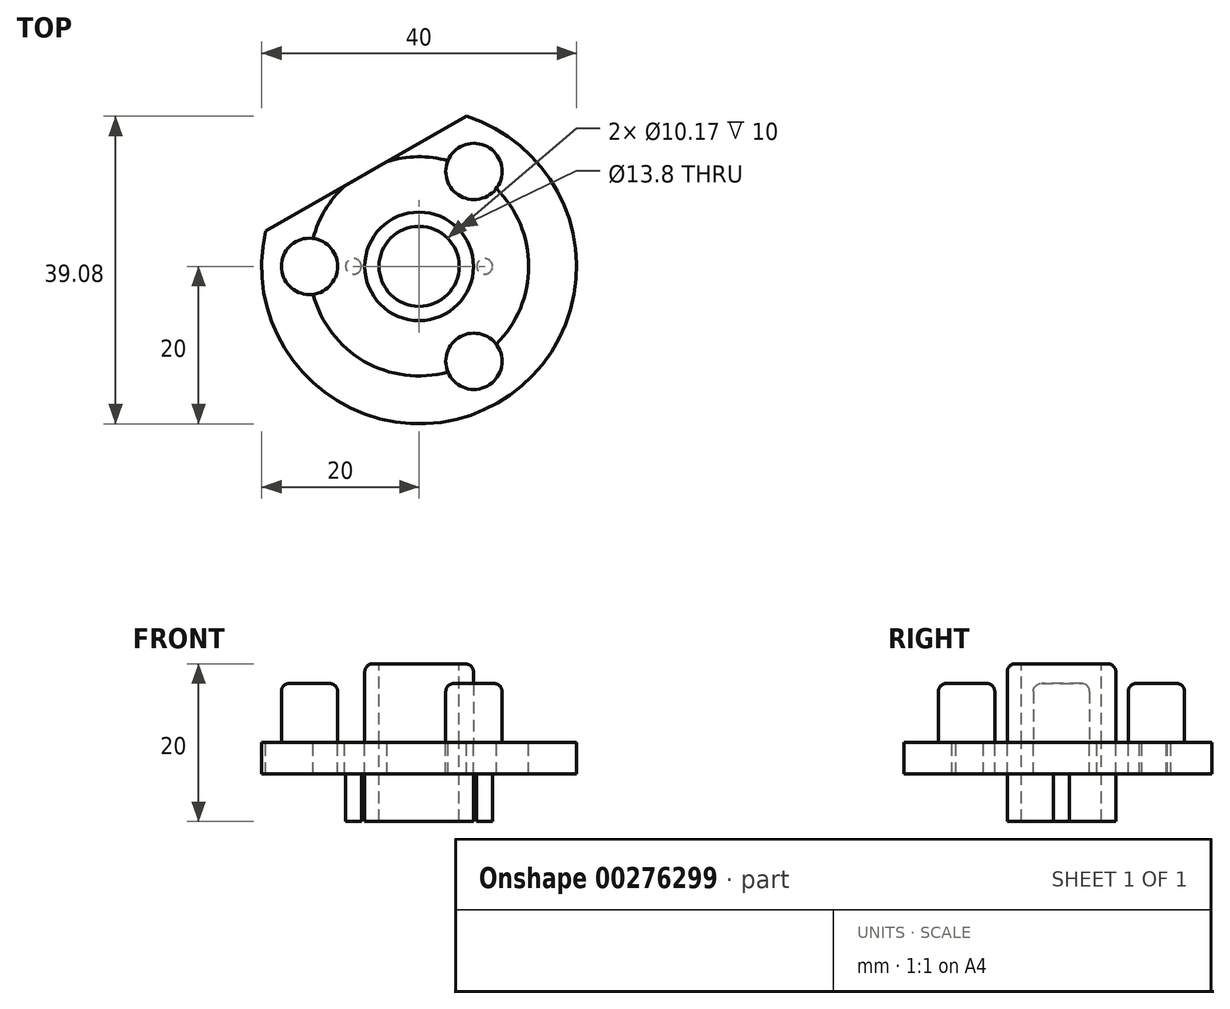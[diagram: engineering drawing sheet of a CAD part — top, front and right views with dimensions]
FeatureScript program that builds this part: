
annotation { "Feature Type Name" : "Feature", "Feature Type Description" : "" }
export const myFeature = defineFeature(function(context is Context, id is Id, definition is map)
    precondition{}
    {
        {
            var Q0;
            Q0=qCreatedBy(makeId("Top.planeOp"),FACE);
            var sketch = newSketch(context, id + "F0", { "sketchPlane" : qUnion([Q0])});
            skCircle(sketch, "E0", {"center": v(0, 0) * mm, "radius": 6.9 * mm});
            skCircle(sketch, "E1", {"center": v(0, 0) * mm, "radius": 20 * mm});
            skSolve(sketch);
        }
        {
            var Q0;
            Q0=qCreatedBy(makeId("Top.planeOp"),FACE);
            var sketch = newSketch(context, id + "F1", { "sketchPlane" : qUnion([Q0])});
            skCircle(sketch, "E2", {"center": v(0, 0) * mm, "radius": 17.5 * mm});
            skCircle(sketch, "E3", {"center": v(0, 0) * mm, "radius": 13.93 * mm});
            skCircle(sketch, "E4", {"center": v(-13.93, 0) * mm, "radius": 3.58 * mm});
            skCircle(sketch, "E5.1.0", {"center": v(6.96, -12.06) * mm, "radius": 3.58 * mm});
            skCircle(sketch, "E5.2.0", {"center": v(6.96, 12.06) * mm, "radius": 3.58 * mm});
            skSolve(sketch);
        }
        {
            var Q0;
            {var subQ0=sQuery(id+"F1.wireOp",EDGE,"E5.2.0");var subQ1=sQuery(id+"F1.wireOp",EDGE,"E3");var subQ2=makeQuery(id+"F1.imprint","INTERSECT",VERTEX,{"disambiguationData":[OD(0.0)],"derivedFrom":[subQ1,subQ0]});Q0=makeQuery(id+"F1.imprint","IMPRINT",FACE,{"disambiguationData":[TD([[makeQuery(id+"F1.imprint","IMPRINT",EDGE,{"disambiguationData":[TD([[subQ2,1.0]])],"derivedFrom":subQ1}),-1.0]])]});}
            var Q1;
            {var subQ0=sQuery(id+"F1.wireOp",EDGE,"E5.2.0");var subQ1=sQuery(id+"F1.wireOp",EDGE,"E3");var subQ2=makeQuery(id+"F1.imprint","INTERSECT",VERTEX,{"disambiguationData":[OD(0.0)],"derivedFrom":[subQ1,subQ0]});Q1=makeQuery(id+"F1.imprint","IMPRINT",FACE,{"disambiguationData":[TD([[makeQuery(id+"F1.imprint","IMPRINT",EDGE,{"disambiguationData":[TD([[subQ2,1.0]])],"derivedFrom":subQ1}),1.0]])]});}
            extrude(context, id + "F2", {"entities" : qUnion([Q0, Q1]), "depth" : 7.5 * mm});
        }
        {
            var Q0;
            {var subQ0=sQuery(id+"F1.wireOp",EDGE,"E4");var subQ1=sQuery(id+"F1.wireOp",EDGE,"E3");var subQ2=makeQuery(id+"F1.imprint","INTERSECT",VERTEX,{"disambiguationData":[OD(0.0)],"derivedFrom":[subQ1,subQ0]});Q0=makeQuery(id+"F1.imprint","IMPRINT",FACE,{"disambiguationData":[TD([[makeQuery(id+"F1.imprint","IMPRINT",EDGE,{"disambiguationData":[TD([[subQ2,-1.0]])],"derivedFrom":subQ1}),-1.0]])]});}
            var Q1;
            {var subQ0=sQuery(id+"F1.wireOp",EDGE,"E4");var subQ1=sQuery(id+"F1.wireOp",EDGE,"E3");var subQ2=makeQuery(id+"F1.imprint","INTERSECT",VERTEX,{"disambiguationData":[OD(0.0)],"derivedFrom":[subQ1,subQ0]});Q1=makeQuery(id+"F1.imprint","IMPRINT",FACE,{"disambiguationData":[TD([[makeQuery(id+"F1.imprint","IMPRINT",EDGE,{"disambiguationData":[TD([[subQ2,-1.0]])],"derivedFrom":subQ1}),1.0]])]});}
            var Q2;
            {var subQ0=sQuery(id+"F1.wireOp",EDGE,"E5.1.0");var subQ1=sQuery(id+"F1.wireOp",EDGE,"E3");var subQ2=makeQuery(id+"F1.imprint","INTERSECT",VERTEX,{"disambiguationData":[OD(0.0)],"derivedFrom":[subQ1,subQ0]});Q2=makeQuery(id+"F1.imprint","IMPRINT",FACE,{"disambiguationData":[TD([[makeQuery(id+"F1.imprint","IMPRINT",EDGE,{"disambiguationData":[TD([[subQ2,-1.0]])],"derivedFrom":subQ1}),1.0]])]});}
            var Q3;
            {var subQ0=sQuery(id+"F1.wireOp",EDGE,"E5.1.0");var subQ1=sQuery(id+"F1.wireOp",EDGE,"E3");var subQ2=makeQuery(id+"F1.imprint","INTERSECT",VERTEX,{"disambiguationData":[OD(0.0)],"derivedFrom":[subQ1,subQ0]});Q3=makeQuery(id+"F1.imprint","IMPRINT",FACE,{"disambiguationData":[TD([[makeQuery(id+"F1.imprint","IMPRINT",EDGE,{"disambiguationData":[TD([[subQ2,-1.0]])],"derivedFrom":subQ1}),-1.0]])]});}
            extrude(context, id + "F3", {"entities" : qUnion([Q0, Q1, Q2, Q3]), "depth" : 7.5 * mm});
        }
        {
            var Q0;
            Q0=makeQuery(id+"F0.imprint","IMPRINT",FACE,{"disambiguationData":[TD([[makeQuery(id+"F0.imprint","IMPRINT",EDGE,{"derivedFrom":sQuery(id+"F0.wireOp",EDGE,"E0")}),1.0]])]});
            extrude(context, id + "F4", {"entities" : qUnion([Q0]), "depth" : 10 * mm});
        }
        {
            var Q0;
            Q0=makeQuery(id+"F0.imprint","IMPRINT",FACE,{"disambiguationData":[TD([[makeQuery(id+"F0.imprint","IMPRINT",EDGE,{"derivedFrom":sQuery(id+"F0.wireOp",EDGE,"E0")}),-1.0]])]});
            var Q1;
            {var subQ0=sQuery(id+"F1.wireOp",EDGE,"E5.2.0");var subQ1=sQuery(id+"F1.wireOp",EDGE,"E3");var subQ9=makeQuery(id+"F1.imprint","INTERSECT",VERTEX,{"disambiguationData":[OD(0.0)],"derivedFrom":[subQ1,subQ0]});Q1=makeQuery(id+"F1.imprint","IMPRINT",FACE,{"disambiguationData":[TD([[makeQuery(id+"F1.imprint","IMPRINT",EDGE,{"disambiguationData":[TD([[subQ9,-1.0]])],"derivedFrom":subQ1}),1.0]])]});}
            extrude(context, id + "F5", {"entities" : qUnion([Q0, Q1]), "oppositeDirection" : true, "depth" : 10 * mm});
        }
        {
            var Q0;
            Q0=makeQuery(id+"F4.opExtrude","CAP_FACE",FACE,{"disambiguationData":[OSD([sQuery(id+"F0.wireOp",EDGE,"E0")])],"isStart":false});
            var sketch = newSketch(context, id + "F6", { "sketchPlane" : qUnion([Q0])});
            skCircle(sketch, "E6", {"center": v(0, 0) * mm, "radius": 5.08 * mm});
            skSolve(sketch);
        }
        {
            var Q0;
            Q0=makeQuery(id+"F6.imprint","IMPRINT",FACE,{"disambiguationData":[TD([[makeQuery(id+"F6.imprint","IMPRINT",EDGE,{"derivedFrom":sQuery(id+"F6.wireOp",EDGE,"E6")}),1.0]])]});
            extrude(context, id + "F7", {"entities" : qUnion([Q0]), "operationType" : NewBodyOperationType.REMOVE, "oppositeDirection" : true, "depth" : 25 * mm});
        }
        {
            var Q0;
            Q0=makeQuery(id+"F5.opExtrude","CAP_FACE",FACE,{"disambiguationData":[OSD([sQuery(id+"F0.wireOp",EDGE,"E0"),sQuery(id+"F0.wireOp",EDGE,"E1")])],"isStart":false});
            var sketch = newSketch(context, id + "F8", { "sketchPlane" : qUnion([Q0])});
            skCircle(sketch, "E7", {"center": v(0, 0) * mm, "radius": 8.32 * mm});
            skCircle(sketch, "E8", {"center": v(0, 8.32) * mm, "radius": 1 * mm});
            skCircle(sketch, "E9.1.0", {"center": v(-8.32, 0) * mm, "radius": 1 * mm});
            skCircle(sketch, "E9.2.0", {"center": v(0, -8.32) * mm, "radius": 1 * mm});
            skCircle(sketch, "E9.3.0", {"center": v(8.32, 0) * mm, "radius": 1 * mm});
            skSolve(sketch);
        }
        {
            var Q0;
            {var subQ0=sQuery(id+"F8.wireOp",EDGE,"E9.1.0");var subQ1=sQuery(id+"F8.wireOp",EDGE,"E7");var subQ2=makeQuery(id+"F8.imprint","INTERSECT",VERTEX,{"disambiguationData":[OD(0.0)],"derivedFrom":[subQ1,subQ0]});Q0=makeQuery(id+"F8.imprint","IMPRINT",FACE,{"disambiguationData":[TD([[makeQuery(id+"F8.imprint","IMPRINT",EDGE,{"disambiguationData":[TD([[subQ2,-1.0]])],"derivedFrom":subQ1}),-1.0]])]});}
            var Q1;
            {var subQ0=sQuery(id+"F8.wireOp",EDGE,"E9.1.0");var subQ1=sQuery(id+"F8.wireOp",EDGE,"E7");var subQ2=makeQuery(id+"F8.imprint","INTERSECT",VERTEX,{"disambiguationData":[OD(0.0)],"derivedFrom":[subQ1,subQ0]});Q1=makeQuery(id+"F8.imprint","IMPRINT",FACE,{"disambiguationData":[TD([[makeQuery(id+"F8.imprint","IMPRINT",EDGE,{"disambiguationData":[TD([[subQ2,-1.0]])],"derivedFrom":subQ1}),1.0]])]});}
            var Q2;
            {var subQ0=sQuery(id+"F8.wireOp",EDGE,"E8");var subQ1=sQuery(id+"F8.wireOp",EDGE,"E7");var subQ2=makeQuery(id+"F8.imprint","INTERSECT",VERTEX,{"disambiguationData":[OD(0.0)],"derivedFrom":[subQ1,subQ0]});Q2=makeQuery(id+"F8.imprint","IMPRINT",FACE,{"disambiguationData":[TD([[makeQuery(id+"F8.imprint","IMPRINT",EDGE,{"disambiguationData":[TD([[subQ2,-1.0]])],"derivedFrom":subQ1}),-1.0]])]});}
            var Q3;
            {var subQ0=sQuery(id+"F8.wireOp",EDGE,"E8");var subQ1=sQuery(id+"F8.wireOp",EDGE,"E7");var subQ2=makeQuery(id+"F8.imprint","INTERSECT",VERTEX,{"disambiguationData":[OD(0.0)],"derivedFrom":[subQ1,subQ0]});Q3=makeQuery(id+"F8.imprint","IMPRINT",FACE,{"disambiguationData":[TD([[makeQuery(id+"F8.imprint","IMPRINT",EDGE,{"disambiguationData":[TD([[subQ2,-1.0]])],"derivedFrom":subQ1}),1.0]])]});}
            var Q4;
            {var subQ0=sQuery(id+"F8.wireOp",EDGE,"E9.3.0");var subQ1=sQuery(id+"F8.wireOp",EDGE,"E7");var subQ2=makeQuery(id+"F8.imprint","INTERSECT",VERTEX,{"disambiguationData":[OD(0.0)],"derivedFrom":[subQ1,subQ0]});Q4=makeQuery(id+"F8.imprint","IMPRINT",FACE,{"disambiguationData":[TD([[makeQuery(id+"F8.imprint","IMPRINT",EDGE,{"disambiguationData":[TD([[subQ2,1.0]])],"derivedFrom":subQ1}),-1.0]])]});}
            var Q5;
            {var subQ0=sQuery(id+"F8.wireOp",EDGE,"E9.3.0");var subQ1=sQuery(id+"F8.wireOp",EDGE,"E7");var subQ2=makeQuery(id+"F8.imprint","INTERSECT",VERTEX,{"disambiguationData":[OD(0.0)],"derivedFrom":[subQ1,subQ0]});Q5=makeQuery(id+"F8.imprint","IMPRINT",FACE,{"disambiguationData":[TD([[makeQuery(id+"F8.imprint","IMPRINT",EDGE,{"disambiguationData":[TD([[subQ2,1.0]])],"derivedFrom":subQ1}),1.0]])]});}
            var Q6;
            {var subQ0=sQuery(id+"F8.wireOp",EDGE,"E9.2.0");var subQ1=sQuery(id+"F8.wireOp",EDGE,"E7");var subQ2=makeQuery(id+"F8.imprint","INTERSECT",VERTEX,{"disambiguationData":[OD(0.0)],"derivedFrom":[subQ1,subQ0]});Q6=makeQuery(id+"F8.imprint","IMPRINT",FACE,{"disambiguationData":[TD([[makeQuery(id+"F8.imprint","IMPRINT",EDGE,{"disambiguationData":[TD([[subQ2,-1.0]])],"derivedFrom":subQ1}),1.0]])]});}
            var Q7;
            {var subQ0=sQuery(id+"F8.wireOp",EDGE,"E9.2.0");var subQ1=sQuery(id+"F8.wireOp",EDGE,"E7");var subQ2=makeQuery(id+"F8.imprint","INTERSECT",VERTEX,{"disambiguationData":[OD(0.0)],"derivedFrom":[subQ1,subQ0]});Q7=makeQuery(id+"F8.imprint","IMPRINT",FACE,{"disambiguationData":[TD([[makeQuery(id+"F8.imprint","IMPRINT",EDGE,{"disambiguationData":[TD([[subQ2,-1.0]])],"derivedFrom":subQ1}),-1.0]])]});}
            extrude(context, id + "F9", {"entities" : qUnion([Q0, Q1, Q2, Q3, Q4, Q5, Q6, Q7]), "operationType" : NewBodyOperationType.REMOVE, "oppositeDirection" : true, "depth" : 6 * mm});
        }
        {
            var Q0;
            Q0=makeQuery(id+"F3.opExtrude","CAP_EDGE",EDGE,{"disambiguationData":[OSD([sQuery(id+"F1.wireOp",EDGE,"E4")])],"isStart":false});
            var Q1;
            Q1=makeQuery(id+"F2.opExtrude","CAP_EDGE",EDGE,{"disambiguationData":[OSD([sQuery(id+"F1.wireOp",EDGE,"E5.2.0")])],"isStart":false});
            var Q2;
            Q2=makeQuery(id+"F3.opExtrude","CAP_EDGE",EDGE,{"disambiguationData":[OSD([sQuery(id+"F1.wireOp",EDGE,"E5.1.0")])],"isStart":false});
            var Q3;
            Q3=makeQuery(id+"F4.opExtrude","CAP_EDGE",EDGE,{"disambiguationData":[OSD([sQuery(id+"F0.wireOp",EDGE,"E0")])],"isStart":false});
            fillet(context, id + "F10", {"entities" : qUnion([Q0, Q1, Q2, Q3]), "radius" : 1 * mm, "tangentPropagation" : true, "allowEdgeOverflow" : false});
        }
        {
            var Q0;
            Q0=makeQuery(id+"F5.opExtrude","CAP_FACE",FACE,{"disambiguationData":[OSD([sQuery(id+"F0.wireOp",EDGE,"E0"),sQuery(id+"F0.wireOp",EDGE,"E1")])],"isStart":true});
            var sketch = newSketch(context, id + "F11", { "sketchPlane" : qUnion([Q0])});
            skLineSegment(sketch, "E10", {"start": v(-13.95, 0) * mm, "end": v(7.03, 12.02) * mm});
            skLineSegment(sketch, "E11", {"start": v(7.03, 12.02) * mm, "end": v(3.73, 17.78) * mm});
            skLineSegment(sketch, "E12", {"start": v(3.73, 17.78) * mm, "end": v(-25.18, 1.21) * mm});
            skLineSegment(sketch, "E13", {"start": v(-25.18, 1.21) * mm, "end": v(9.33, 21) * mm});
            skSolve(sketch);
        }
        {
            var Q0;
            {var subQ0=sQuery(id+"F11.wireOp",EDGE,"E13");var subQ1=makeQuery(id+"F11.imprint","IMPRINT",VERTEX,{"derivedFrom":subQ0});Q0=makeQuery(id+"F11.imprint","IMPRINT",FACE,{"disambiguationData":[TD([[makeQuery(id+"F11.imprint","IMPRINT",EDGE,{"disambiguationData":[TD([[subQ1,1.0]])],"derivedFrom":subQ0}),1.0]])]});}
            extrude(context, id + "F12", {"entities" : qUnion([Q0]), "operationType" : NewBodyOperationType.REMOVE, "oppositeDirection" : true, "depth" : 25 * mm});
        }
    });
